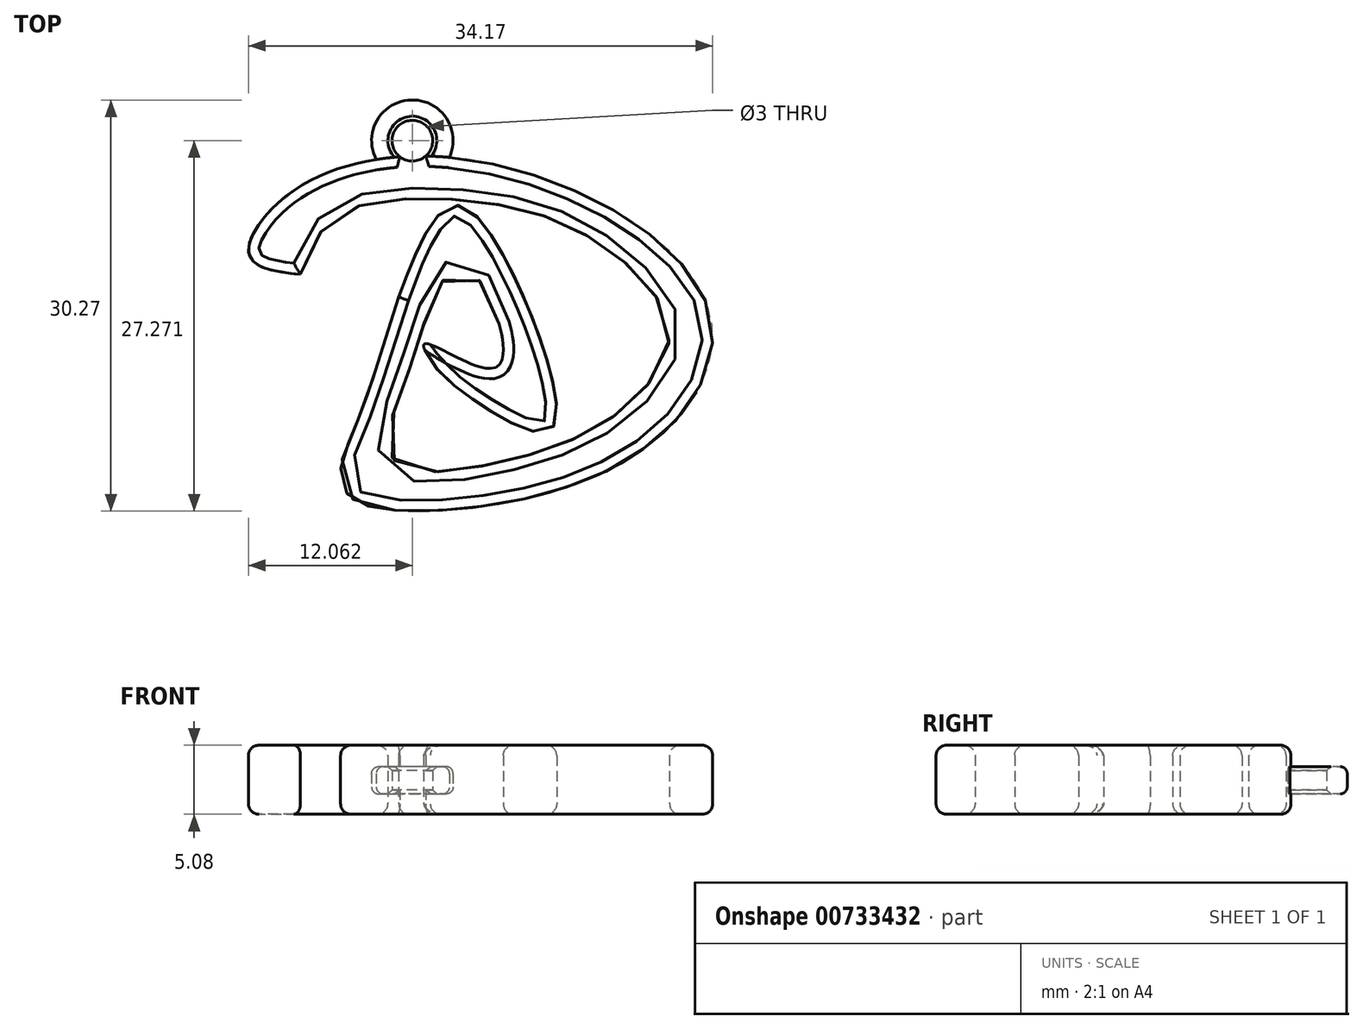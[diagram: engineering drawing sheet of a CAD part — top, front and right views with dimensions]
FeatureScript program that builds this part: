
annotation { "Feature Type Name" : "Feature", "Feature Type Description" : "" }
export const myFeature = defineFeature(function(context is Context, id is Id, definition is map)
    precondition{}
    {
        {
            var Q0;
            Q0=qCreatedBy(makeId("Top.planeOp"),FACE);
            var sketch = newSketch(context, id + "F0", { "sketchPlane" : qUnion([Q0])});
            skFitSpline(sketch, "E0", {"points": [v(-14.62, 14.52) * mm, v(-17.63, 5.43) * mm, v(-18.87, 2.05) * mm, v(-18.38, 0) * mm, v(-14.64, -1.2) * mm, v(2.2, 2.54) * mm, v(8.22, 13.5) * mm, v(-7.15, 24.2) * mm, v(-22.4, 22.33) * mm, v(-25.6, 17.51) * mm, v(-21.86, 16.18) * mm], "startDerivative": vector(-30.16, -90.74) * mm, "endDerivative": vector(73.39, -8.95) * mm});
            skFitSpline(sketch, "E1", {"points": [v(-21.86, 16.18) * mm, v(-19.72, 20.05) * mm, v(-15.3, 21.66) * mm, v(-6.88, 21.26) * mm, v(0, 18.58) * mm, v(4.88, 13.64) * mm, v(4.88, 9.9) * mm, v(0, 4.95) * mm, v(-8.9, 2) * mm, v(-14.37, 2) * mm, v(-15.44, 3.88) * mm, v(-14, 8.76) * mm, v(-11.03, 16.18) * mm, v(-9.02, 16.18) * mm, v(-7.42, 9.36) * mm, v(-12.66, 11.1) * mm, v(-12.26, 9.83) * mm, v(-9.62, 7.31) * mm, v(-4.21, 4.55) * mm, v(-3, 5.75) * mm, v(-6.88, 17.51) * mm, v(-10.63, 21.26) * mm, v(-13.15, 18.2) * mm, v(-14.62, 14.52) * mm], "startDerivative": vector(41, 106.02) * mm, "endDerivative": vector(-36.97, -96.62) * mm});
            skArc(sketch, "E2", {"start": v(-10.88, 24.8) * mm, "mid": v(-13.7, 29.03) * mm, "end": v(-16.28, 24.65) * mm});
            skCircle(sketch, "E3", {"center": v(-13.62, 26.03) * mm, "radius": 1.5 * mm});
            skSolve(sketch);
        }
        {
            var Q0;
            Q0=makeQuery(id+"F0.imprint","IMPRINT",FACE,{"disambiguationData":[TD([[makeQuery(id+"F0.imprint","IMPRINT",EDGE,{"derivedFrom":sQuery(id+"F0.wireOp",EDGE,"E0")}),1.0]])]});
            extrude(context, id + "F1", {"entities" : qUnion([Q0]), "depth" : 5.08 * mm, "offsetDistance" : 25.4 * mm});
        }
        {
            var Q0;
            {var subQ0=sQuery(id+"F0.wireOp",EDGE,"E0");var subQ1=makeQuery(id+"F0.imprint","INTERSECT",VERTEX,{"disambiguationData":[OD(1.0)],"derivedFrom":[subQ0,sQuery(id+"F0.wireOp",EDGE,"E2")]});Q0=makeQuery(id+"F1.opExtrude","CAP_EDGE",EDGE,{"disambiguationData":[OSD([subQ0]),TDD([makeQuery(id+"F0.imprint","IMPRINT",EDGE,{"disambiguationData":[TD([[subQ1,1.0]])],"derivedFrom":subQ0}),makeQuery(id+"F0.imprint","IMPRINT",EDGE,{"disambiguationData":[TD([[makeQuery(id+"F0.imprint","INTERSECT",VERTEX,{"disambiguationData":[OD(1.0)],"derivedFrom":[subQ0,sQuery(id+"F0.wireOp",EDGE,"E1")]}),1.0]])],"derivedFrom":subQ0})])],"isStart":false});}
            var Q1;
            Q1=makeQuery(id+"F1.opExtrude","CAP_EDGE",EDGE,{"disambiguationData":[OSD([sQuery(id+"F0.wireOp",EDGE,"E1")])],"isStart":false});
            var Q2;
            Q2=makeQuery(id+"F1.opExtrude","CAP_EDGE",EDGE,{"disambiguationData":[OSD([sQuery(id+"F0.wireOp",EDGE,"E1")])],"isStart":true});
            var Q3;
            {var subQ0=sQuery(id+"F0.wireOp",EDGE,"E0");var subQ1=makeQuery(id+"F0.imprint","INTERSECT",VERTEX,{"disambiguationData":[OD(0.0)],"derivedFrom":[subQ0,sQuery(id+"F0.wireOp",EDGE,"E2")]});Q3=makeQuery(id+"F1.opExtrude","CAP_EDGE",EDGE,{"disambiguationData":[OSD([subQ0]),TDD([makeQuery(id+"F0.imprint","IMPRINT",EDGE,{"disambiguationData":[TD([[makeQuery(id+"F0.imprint","INTERSECT",VERTEX,{"disambiguationData":[OD(0.0)],"derivedFrom":[subQ0,sQuery(id+"F0.wireOp",EDGE,"E1")]}),-1.0]])],"derivedFrom":subQ0}),makeQuery(id+"F0.imprint","IMPRINT",EDGE,{"disambiguationData":[TD([[subQ1,-1.0]])],"derivedFrom":subQ0})])],"isStart":false});}
            var Q4;
            Q4=makeQuery(id+"F1.opExtrude","CAP_EDGE",EDGE,{"disambiguationData":[OSD([sQuery(id+"F0.wireOp",EDGE,"E3")])],"isStart":false});
            var Q5;
            {var subQ0=sQuery(id+"F0.wireOp",EDGE,"E0");var subQ1=makeQuery(id+"F0.imprint","INTERSECT",VERTEX,{"disambiguationData":[OD(0.0)],"derivedFrom":[subQ0,sQuery(id+"F0.wireOp",EDGE,"E2")]});Q5=makeQuery(id+"F1.opExtrude","CAP_EDGE",EDGE,{"disambiguationData":[OSD([subQ0]),TDD([makeQuery(id+"F0.imprint","IMPRINT",EDGE,{"disambiguationData":[TD([[makeQuery(id+"F0.imprint","INTERSECT",VERTEX,{"disambiguationData":[OD(0.0)],"derivedFrom":[subQ0,sQuery(id+"F0.wireOp",EDGE,"E1")]}),-1.0]])],"derivedFrom":subQ0}),makeQuery(id+"F0.imprint","IMPRINT",EDGE,{"disambiguationData":[TD([[subQ1,-1.0]])],"derivedFrom":subQ0})])],"isStart":true});}
            var Q6;
            Q6=makeQuery(id+"F1.opExtrude","CAP_EDGE",EDGE,{"disambiguationData":[OSD([sQuery(id+"F0.wireOp",EDGE,"E3")])],"isStart":true});
            var Q7;
            {var subQ0=sQuery(id+"F0.wireOp",EDGE,"E0");var subQ1=makeQuery(id+"F0.imprint","INTERSECT",VERTEX,{"disambiguationData":[OD(1.0)],"derivedFrom":[subQ0,sQuery(id+"F0.wireOp",EDGE,"E2")]});Q7=makeQuery(id+"F1.opExtrude","CAP_EDGE",EDGE,{"disambiguationData":[OSD([subQ0]),TDD([makeQuery(id+"F0.imprint","IMPRINT",EDGE,{"disambiguationData":[TD([[subQ1,1.0]])],"derivedFrom":subQ0}),makeQuery(id+"F0.imprint","IMPRINT",EDGE,{"disambiguationData":[TD([[makeQuery(id+"F0.imprint","INTERSECT",VERTEX,{"disambiguationData":[OD(1.0)],"derivedFrom":[subQ0,sQuery(id+"F0.wireOp",EDGE,"E1")]}),1.0]])],"derivedFrom":subQ0})])],"isStart":true});}
            fillet(context, id + "F2", {"entities" : qUnion([Q0, Q1, Q2, Q3, Q4, Q5, Q6, Q7]), "radius" : 0.76 * mm, "tangentPropagation" : true, "allowEdgeOverflow" : false});
        }
        {
            var Q0;
            {var subQ0=sQuery(id+"F0.wireOp",EDGE,"E2");Q0=makeQuery(id+"F0.imprint","IMPRINT",FACE,{"disambiguationData":[TD([[makeQuery(id+"F0.imprint","IMPRINT",EDGE,{"derivedFrom":subQ0}),1.0]])]});}
            extrude(context, id + "F3", {"entities" : qUnion([Q0]), "operationType" : NewBodyOperationType.ADD, "depth" : 3.5 * mm, "offsetDistance" : 25 * mm, "hasSecondDirection" : true, "secondDirectionOppositeDirection" : false, "secondDirectionDepth" : 1.5 * mm});
        }
        {
            var Q0;
            Q0=makeQuery(id+"F3.opExtrude","CAP_EDGE",EDGE,{"disambiguationData":[OSD([sQuery(id+"F0.wireOp",EDGE,"E2")])],"isStart":false});
            var Q1;
            Q1=makeQuery(id+"F3.opExtrude","CAP_EDGE",EDGE,{"disambiguationData":[OSD([sQuery(id+"F0.wireOp",EDGE,"E2")])],"isStart":true});
            fillet(context, id + "F4", {"entities" : qUnion([Q0, Q1]), "radius" : .5 * mm, "tangentPropagation" : true, "allowEdgeOverflow" : false});
        }
        {
            var Q0;
            Q0=makeQuery(id+"F3.opExtrude","CAP_EDGE",EDGE,{"disambiguationData":[OSD([sQuery(id+"F0.wireOp",EDGE,"E3")])],"isStart":false});
            var Q1;
            Q1=makeQuery(id+"F3.opExtrude","CAP_EDGE",EDGE,{"disambiguationData":[OSD([sQuery(id+"F0.wireOp",EDGE,"E3")])],"isStart":true});
            chamfer(context, id + "F5", {"entities" : qUnion([Q0, Q1]), "width" : .3 * mm, "tangentPropagation" : true});
        }
    });
